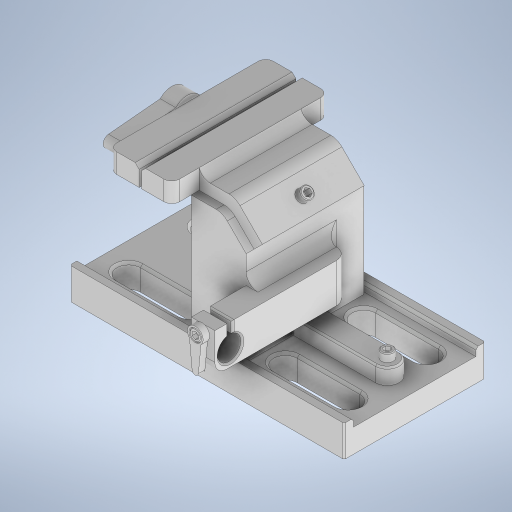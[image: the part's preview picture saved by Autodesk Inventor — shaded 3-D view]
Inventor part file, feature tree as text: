
AUTODESK INVENTOR PART (.ipt)
format: ipt  version: 2024.3 (Build 283343000, 343)  size: 720,384 bytes
history: native  units: mm
features: other x26, extrude x25, sketch x25, chamfer x9, fillet x6, mirror x3
ambient origin geometry x8: Origin, YZ Plane, XZ Plane, XY Plane, X Axis, Y Axis, Z Axis, Center Point
bodies: Solido1 (feature_tree)
feature tree (94):
  extrude  "Estrusione1"  Depth=0.18mm
  extrude  "Estrusione2"  Depth=0.35mm
  extrude  "Estrusione3"  Depth=0.03mm TaperAngle=0.0deg
  extrude  "Estrusione4"  Depth=0.07mm
  extrude  "Estrusione5"  Depth=0.15mm
  mirror  "Speculare1"
  extrude  "Estrusione6"  Depth=0.15mm TaperAngle=0.0deg
  extrude  "Estrusione7"  Depth=0.03mm
  extrude  "Estrusione8"  Depth=0.12mm
  extrude  "Estrusione9"  Depth=0.02mm TaperAngle=0.0deg
  extrude  "Estrusione10"  Depth=0.03mm
  extrude  "Estrusione11"  Depth=0.03mm
  extrude  "Estrusione12"  TaperAngle=0.0deg  [1 undecoded]
  extrude  "Estrusione13"  Depth=0.012mm
  extrude  "Estrusione14"  Depth=0.01mm TaperAngle=0.0deg
  extrude  "Estrusione15"  Depth=0.05mm
  mirror  "Speculare2"
  mirror  "Speculare3"
  fillet  "Raccordo1"  Radius=0.05mm
  chamfer  "Smusso1"  Distance=0.17mm
  chamfer  "Smusso2"  Distance=0.03mm
  chamfer  "Smusso3"  Distance=0.015mm
  fillet  "Raccordo2"  Radius=0.015mm
  fillet  "Raccordo3"  Radius=0.13mm
  chamfer  "Smusso4"  Distance=0.025mm
  fillet  "Raccordo4"  Radius=0.2mm
  fillet  "Raccordo5"  Radius=0.08mm
  chamfer  "Smusso5"  Distance=0.003mm
  other  "Piano di lavoro1"
  extrude  "Estrusione16"  TaperAngle=0.0deg  [1 undecoded]
  fillet  "Raccordo6"  Radius=0.04mm
  extrude  "Estrusione17"  Depth=0.1mm
  extrude  "Estrusione18"  Depth=0.015mm
  extrude  "Estrusione19"  Depth=0.02mm TaperAngle=0.0deg
  chamfer  "Smusso6"  Distance=0.015mm
  extrude  "Estrusione20"  Depth=0.08mm
  extrude  "Estrusione21"  Depth=0.12mm
  extrude  "Estrusione22"  Depth=0.005mm TaperAngle=0.0deg
  chamfer  "Smusso7"  Distance=0.03mm
  extrude  "Estrusione23"  Depth=0.02mm
  chamfer  "Smusso8"  Distance=0.02mm
  extrude  "Estrusione24"  TaperAngle=0.0deg  [1 undecoded]
  extrude  "Estrusione25"  Depth=0.005mm
  chamfer  "Smusso9"  [1 undecoded]
  sketch  "Schizzo1"
  sketch  "Schizzo2"
  other  "Linea chiusa proiettata1"
  sketch  "Schizzo3"
  other  "Linea chiusa proiettata2"
  other  "Linea chiusa proiettata3"
  sketch  "Schizzo4"
  other  "Linea chiusa proiettata4"
  sketch  "Schizzo5"
  other  "Linea chiusa proiettata5"
  other  "Linea chiusa proiettata6"
  sketch  "Schizzo6"
  other  "Linea chiusa proiettata7"
  sketch  "Schizzo7"
  other  "Linea chiusa proiettata8"
  sketch  "Schizzo8"
  other  "Linea chiusa proiettata9"
  sketch  "Schizzo10"
  other  "Linea chiusa proiettata11"
  sketch  "Schizzo11"
  other  "Linea chiusa proiettata12"
  sketch  "Schizzo12"
  other  "Linea chiusa proiettata13"
  other  "Linea chiusa proiettata14"
  sketch  "Schizzo14"
  other  "Linea chiusa proiettata16"
  sketch  "Schizzo15"
  other  "Linea chiusa proiettata17"
  sketch  "Schizzo16"
  sketch  "Schizzo17"
  other  "Linea chiusa proiettata18"
  sketch  "Schizzo18"
  other  "Linea chiusa proiettata19"
  sketch  "Schizzo19"
  other  "Linea chiusa proiettata20"
  sketch  "Schizzo20"
  other  "Linea chiusa proiettata21"
  sketch  "Schizzo21"
  other  "Linea chiusa proiettata22"
  sketch  "Schizzo22"
  sketch  "Schizzo23"
  other  "Linea chiusa proiettata23"
  sketch  "Schizzo24"
  other  "Linea chiusa proiettata24"
  sketch  "Schizzo25"
  other  "Linea chiusa proiettata25"
  sketch  "Schizzo26"
  other  "Linea chiusa proiettata26"
  sketch  "Schizzo27"
  other  "Linea chiusa proiettata27"
note: 4 required parameter values undecoded (feature->parameter linkage not recoverable at this tier; creation-order binding heuristic only, values carry confidence <= 0.55)
